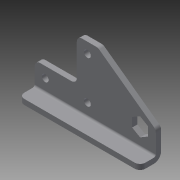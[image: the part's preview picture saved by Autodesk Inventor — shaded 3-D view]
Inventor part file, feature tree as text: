
AUTODESK INVENTOR PART (.ipt)
format: ipt  version: 2014 (Build 180170000, 170)  size: 138,240 bytes
history: native  units: in
note: dims shown in document units (in); Inventor stores cm internally (conversion verified against a paired STEP export)
features: sheet_metal_op x4, sketch x2, other x2, fillet x1
ambient origin geometry x8: Origin, YZ Plane, XZ Plane, XY Plane, X Axis, Y Axis, Z Axis, Center Point
bodies: Solid1 (feature_tree)
feature tree (9):
  sheet_metal_op  "Face1"
  sheet_metal_op  "Flange1"
  fillet  "Fillet2"  Radius=0.5in
  sketch  "Sketch1"  dims[d1=1.0in]
  other  "Plate1"
  sketch  "Sketch2"  dims[d2=1.0in d3=0.5in d4=2.875in d5=0.375in d6=0.375in d7=0.375in d8=90.0deg d9=0.5in d10=0.163in d11=0.25in d12=0.25in d13=0.7874in d15=1.0in d16=0.3937in d18=1.0in d20=0.7874in d22=1.0in d23=0.3937in d25=1.0in d27=0.125in d29=0.125in d30=0.0625in d31=0.25in d32=0.125in d33=0.5in d34=90.0deg d35=0.05in d36=0.5in d37=0.125in d38=0.125in d39=0.125in]
  other  "Plate2"
  sheet_metal_op  "Bend1"
  sheet_metal_op  "Corner1"
